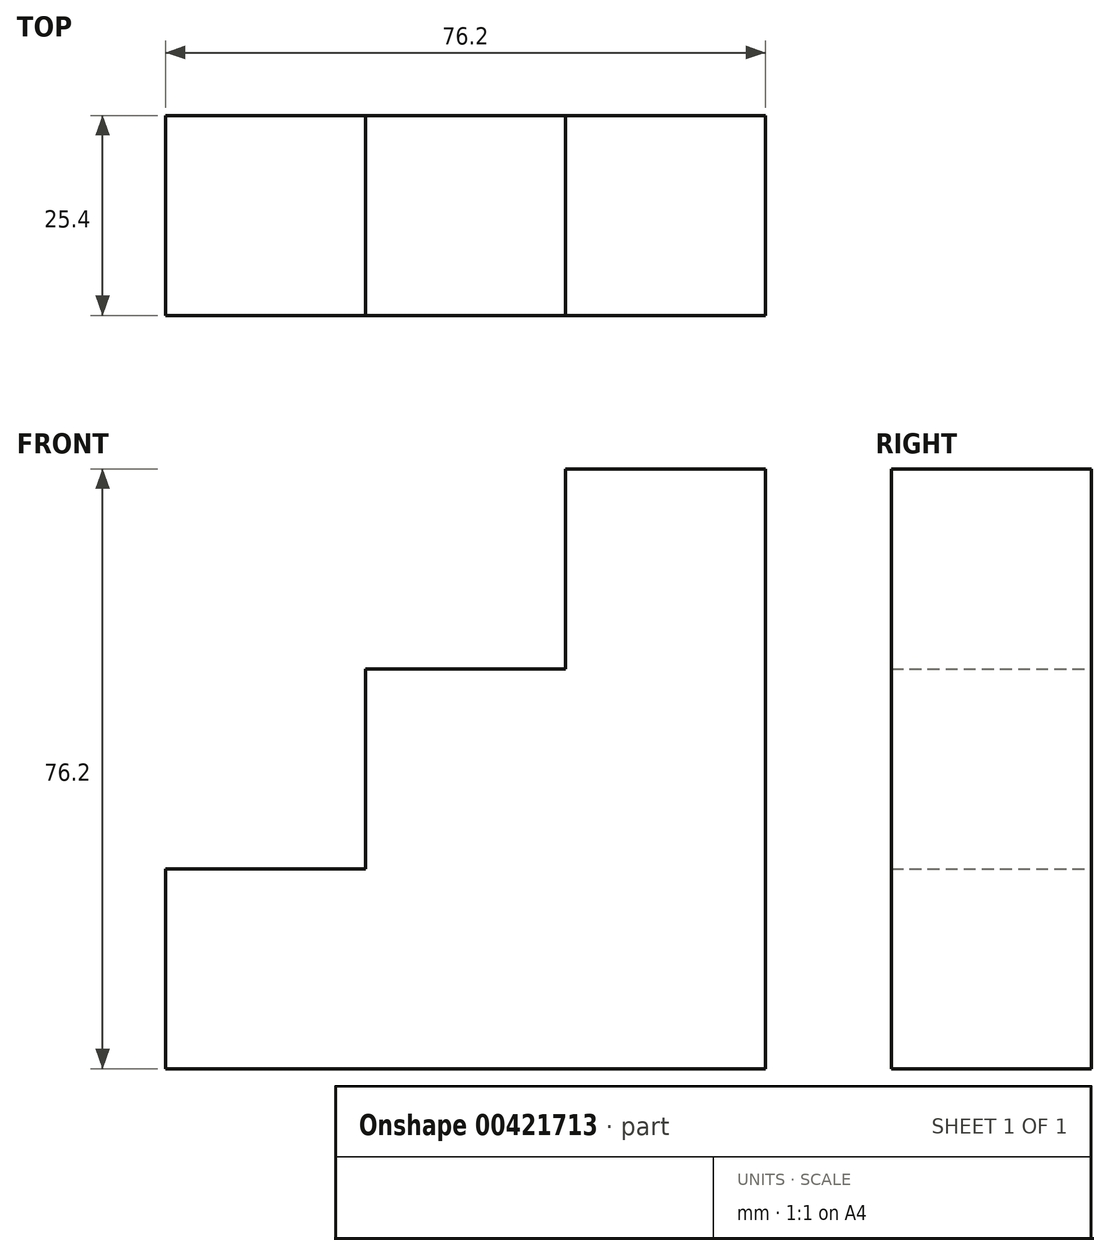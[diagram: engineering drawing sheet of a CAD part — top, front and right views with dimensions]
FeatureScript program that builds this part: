
annotation { "Feature Type Name" : "Feature", "Feature Type Description" : "" }
export const myFeature = defineFeature(function(context is Context, id is Id, definition is map)
    precondition{}
    {
        {
            var Q0;
            Q0=qCreatedBy(makeId("Front.planeOp"),FACE);
            var sketch = newSketch(context, id + "F0", { "sketchPlane" : qUnion([Q0])});
            skLineSegment(sketch, "E0", {"start": v(39.44, 0) * mm, "end": v(-36.76, 0) * mm});
            skLineSegment(sketch, "E1", {"start": v(-36.76, 0) * mm, "end": v(-36.76, 25.4) * mm});
            skLineSegment(sketch, "E2", {"start": v(-36.76, 25.4) * mm, "end": v(-11.36, 25.4) * mm});
            skLineSegment(sketch, "E3", {"start": v(-11.36, 25.4) * mm, "end": v(-11.36, 50.8) * mm});
            skLineSegment(sketch, "E4", {"start": v(-11.36, 50.8) * mm, "end": v(14.04, 50.8) * mm});
            skLineSegment(sketch, "E5", {"start": v(14.04, 50.8) * mm, "end": v(14.04, 76.2) * mm});
            skLineSegment(sketch, "E6", {"start": v(14.04, 76.2) * mm, "end": v(39.44, 76.2) * mm});
            skLineSegment(sketch, "E7", {"start": v(39.44, 76.2) * mm, "end": v(39.44, 0) * mm});
            skSolve(sketch);
        }
        {
            var Q0;
            Q0=makeQuery(id+"F0.imprint","IMPRINT",FACE,{"disambiguationData":[TD([[makeQuery(id+"F0.imprint","IMPRINT",EDGE,{"derivedFrom":sQuery(id+"F0.wireOp",EDGE,"E0")}),-1.0]])]});
            extrude(context, id + "F1", {"entities" : qUnion([Q0]), "depth" : 25.4 * mm});
        }
    });
